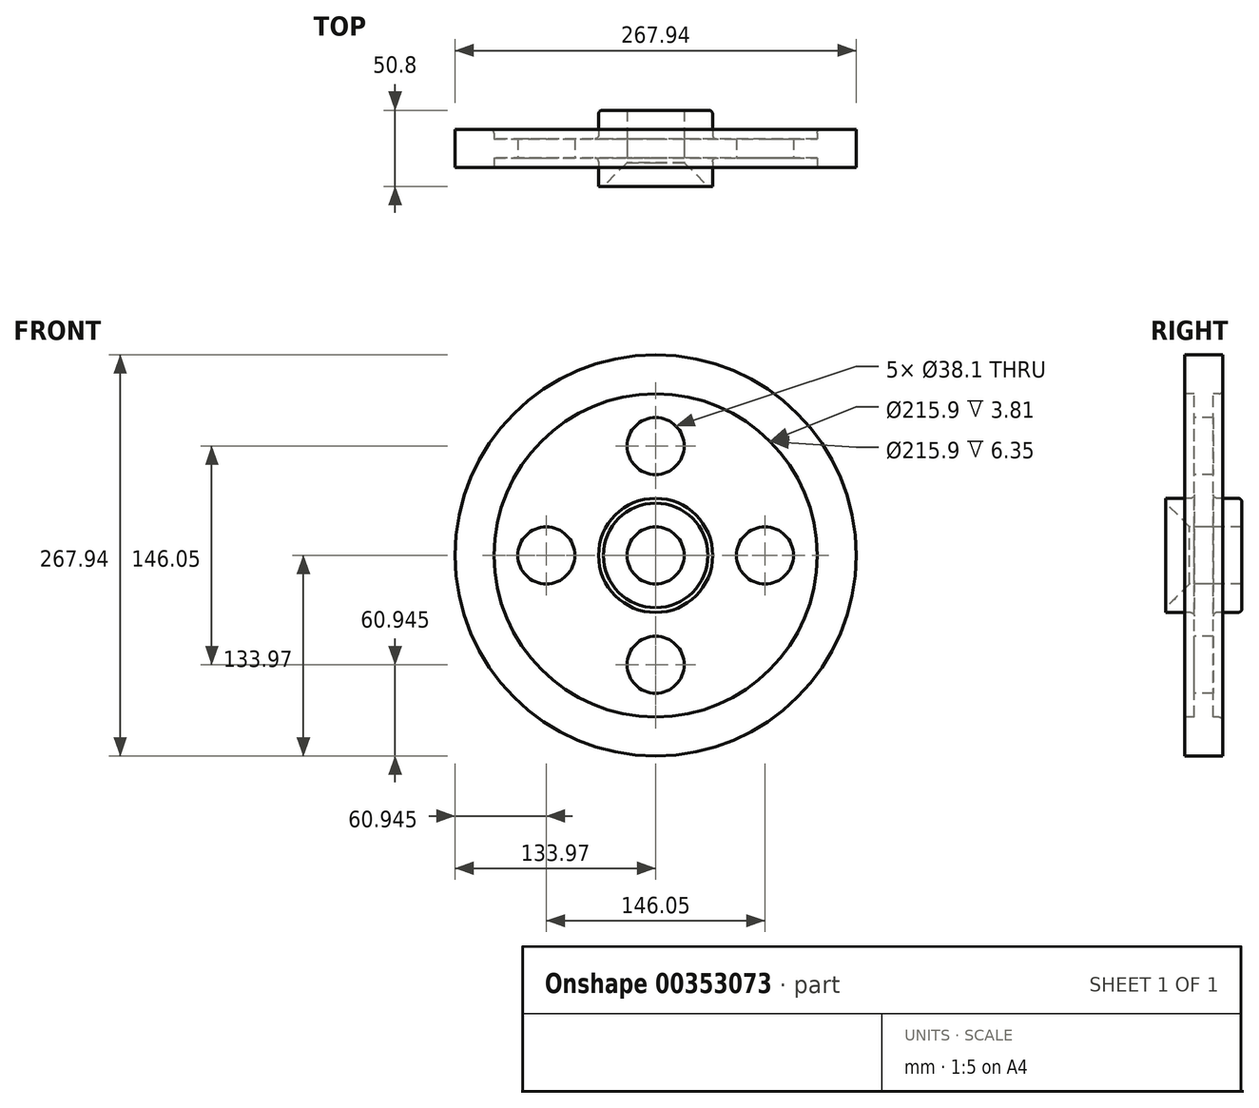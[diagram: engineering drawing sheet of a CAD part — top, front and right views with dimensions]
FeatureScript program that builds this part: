
annotation { "Feature Type Name" : "Feature", "Feature Type Description" : "" }
export const myFeature = defineFeature(function(context is Context, id is Id, definition is map)
    precondition{}
    {
        {
            var Q0;
            Q0=qCreatedBy(makeId("Right.planeOp"),FACE);
            var sketch = newSketch(context, id + "F0", { "sketchPlane" : qUnion([Q0])});
            skLineSegment(sketch, "E0", {"start": v(0, 0) * mm, "end": v(77.21, 0) * mm, "construction": true});
            skLineSegment(sketch, "E1.0", {"start": v(0, 19.05) * mm, "end": v(25.4, 19.05) * mm});
            skLineSegment(sketch, "E2.0", {"start": v(6.35, 38.1) * mm, "end": v(12.7, 38.1) * mm});
            skLineSegment(sketch, "E3.0", {"start": v(0, 133.35) * mm, "end": v(6.35, 133.35) * mm, "construction": true});
            skLineSegment(sketch, "E4", {"start": v(0, 133.35) * mm, "end": v(0, 0) * mm, "construction": true});
            skLineSegment(sketch, "E5.0", {"start": v(25.4, 19.05) * mm, "end": v(25.4, 0) * mm});
            skLineSegment(sketch, "E6.0", {"start": v(6.35, 107.95) * mm, "end": v(6.35, 38.1) * mm});
            skLineSegment(sketch, "E7", {"start": v(12.7, 107.95) * mm, "end": v(12.7, 133.97) * mm});
            skLineSegment(sketch, "E8", {"start": v(25.4, 19.05) * mm, "end": v(25.4, 38.1) * mm});
            skLineSegment(sketch, "E9", {"start": v(12.7, 38.1) * mm, "end": v(25.4, 38.1) * mm});
            skLineSegment(sketch, "E10", {"start": v(6.35, 107.95) * mm, "end": v(12.7, 107.95) * mm});
            skLineSegment(sketch, "E11.MirrorCS", {"start": v(0, 133.35) * mm, "end": v(-6.35, 133.35) * mm, "construction": true});
            skLineSegment(sketch, "E12.MirrorCS", {"start": v(-12.7, 107.95) * mm, "end": v(-12.7, 133.97) * mm});
            skLineSegment(sketch, "E13.MirrorCS", {"start": v(-6.35, 107.95) * mm, "end": v(-12.7, 107.95) * mm});
            skLineSegment(sketch, "E14.MirrorCS", {"start": v(-6.35, 107.95) * mm, "end": v(-6.35, 38.1) * mm});
            skLineSegment(sketch, "E15.MirrorCS", {"start": v(-12.7, 38.1) * mm, "end": v(-25.4, 38.1) * mm});
            skLineSegment(sketch, "E16.MirrorCS", {"start": v(-6.35, 38.1) * mm, "end": v(-12.7, 38.1) * mm});
            skLineSegment(sketch, "E17.MirrorCS", {"start": v(-25.4, 19.05) * mm, "end": v(-25.4, 38.1) * mm});
            skLineSegment(sketch, "E18.MirrorCS", {"start": v(0, 19.05) * mm, "end": v(-25.4, 19.05) * mm});
            skLineSegment(sketch, "E19", {"start": v(-12.7, 133.97) * mm, "end": v(-6.35, 133.35) * mm, "construction": true});
            skLineSegment(sketch, "E20", {"start": v(-9.53, 38.1) * mm, "end": v(-6.35, 38.1) * mm, "construction": true});
            skLineSegment(sketch, "E21", {"start": v(12.7, 38.1) * mm, "end": v(6.35, 38.1) * mm, "construction": true});
            skLineSegment(sketch, "E22", {"start": v(6.35, 133.35) * mm, "end": v(12.7, 133.97) * mm, "construction": true});
            skLineSegment(sketch, "E23", {"start": v(6.35, 133.35) * mm, "end": v(0, 133.35) * mm, "construction": true});
            skLineSegment(sketch, "E24", {"start": v(-6.35, 133.35) * mm, "end": v(0, 133.35) * mm, "construction": true});
            skLineSegment(sketch, "E25", {"start": v(-6.35, 133.35) * mm, "end": v(-12.7, 133.97) * mm, "construction": true});
            skLineSegment(sketch, "E26", {"start": v(-12.7, 133.97) * mm, "end": v(12.7, 133.97) * mm});
            skSolve(sketch);
        }
        {
            var Q0;
            Q0=makeQuery(id+"F0.imprint","IMPRINT",FACE,{"disambiguationData":[TD([[makeQuery(id+"F0.imprint","IMPRINT",EDGE,{"derivedFrom":sQuery(id+"F0.wireOp",EDGE,"E1.0")}),1.0]])]});
            var Q1;
            Q1=sQuery(id+"F0.wireOp",EDGE,"E0");
            revolve(context, id + "F1", {"entities" : qUnion([Q0]), "axis" : qUnion([Q1]), "revolveType" : RevolveType.FULL});
        }
        {
            var Q0;
            Q0=makeQuery(id+"F1.opRevolve","SWEPT_FACE",FACE,{"disambiguationData":[OSD([sQuery(id+"F0.wireOp",EDGE,"E14.MirrorCS")])]});
            var sketch = newSketch(context, id + "F2", { "sketchPlane" : qUnion([Q0])});
            skLineSegment(sketch, "E27", {"start": v(0, 0) * mm, "end": v(0, 73.03) * mm});
            skCircle(sketch, "E28", {"center": v(0, 73.03) * mm, "radius": 19.05 * mm});
            skCircle(sketch, "E29.1.0", {"center": v(-73.03, 0) * mm, "radius": 19.05 * mm});
            skCircle(sketch, "E29.2.0", {"center": v(0, -73.03) * mm, "radius": 19.05 * mm});
            skCircle(sketch, "E29.3.0", {"center": v(73.03, 0) * mm, "radius": 19.05 * mm});
            skPoint(sketch, "E29.center", {"position": v(0, 0) * mm});
            skSolve(sketch);
        }
        {
            var Q0;
            Q0=makeQuery(id+"F2.imprint","IMPRINT",FACE,{"disambiguationData":[TD([[makeQuery(id+"F2.imprint","IMPRINT",EDGE,{"derivedFrom":sQuery(id+"F2.wireOp",EDGE,"E29.3.0")}),1.0]])]});
            var Q1;
            Q1=makeQuery(id+"F2.imprint","IMPRINT",FACE,{"disambiguationData":[TD([[makeQuery(id+"F2.imprint","IMPRINT",EDGE,{"derivedFrom":sQuery(id+"F2.wireOp",EDGE,"E29.1.0")}),1.0]])]});
            var Q2;
            Q2=makeQuery(id+"F2.imprint","IMPRINT",FACE,{"disambiguationData":[TD([[makeQuery(id+"F2.imprint","IMPRINT",EDGE,{"derivedFrom":sQuery(id+"F2.wireOp",EDGE,"E28")}),1.0]])]});
            var Q3;
            Q3=makeQuery(id+"F2.imprint","IMPRINT",FACE,{"disambiguationData":[TD([[makeQuery(id+"F2.imprint","IMPRINT",EDGE,{"derivedFrom":sQuery(id+"F2.wireOp",EDGE,"E29.2.0")}),1.0]])]});
            extrude(context, id + "F3", {"entities" : qUnion([Q0, Q1, Q2, Q3]), "operationType" : NewBodyOperationType.REMOVE, "oppositeDirection" : true, "depth" : 25.4 * mm});
        }
        {
            var Q0;
            Q0=makeQuery(id+"F1.opRevolve","SWEPT_EDGE",EDGE,{"disambiguationData":[OSD([sQuery(id+"F0.wireOp",EDGE,"E14.MirrorCS"),sQuery(id+"F0.wireOp",EDGE,"E16.MirrorCS")])]});
            var Q1;
            Q1=makeQuery(id+"F1.opRevolve","SWEPT_EDGE",EDGE,{"disambiguationData":[OSD([sQuery(id+"F0.wireOp",EDGE,"E8"),sQuery(id+"F0.wireOp",EDGE,"E9")])]});
            var Q2;
            Q2=makeQuery(id+"F1.opRevolve","SWEPT_FACE",FACE,{"disambiguationData":[OSD([sQuery(id+"F0.wireOp",EDGE,"E2.0"),sQuery(id+"F0.wireOp",EDGE,"E9")])]});
            var Q3;
            Q3=makeQuery(id+"F1.opRevolve","SWEPT_EDGE",EDGE,{"disambiguationData":[OSD([sQuery(id+"F0.wireOp",EDGE,"E7"),sQuery(id+"F0.wireOp",EDGE,"E10")])]});
            fillet(context, id + "F4", {"entities" : qUnion([Q0, Q1, Q2, Q3]), "radius" : 2.54 * mm, "tangentPropagation" : true, "allowEdgeOverflow" : false});
        }
        {
            var Q0;
            Q0=makeQuery(id+"F1.opRevolve","SWEPT_EDGE",EDGE,{"disambiguationData":[OSD([sQuery(id+"F0.wireOp",EDGE,"E17.MirrorCS"),sQuery(id+"F0.wireOp",EDGE,"E18.MirrorCS")])]});
            chamfer(context, id + "F5", {"entities" : qUnion([Q0]), "width" : 15.88 * mm, "tangentPropagation" : true});
        }
    });
